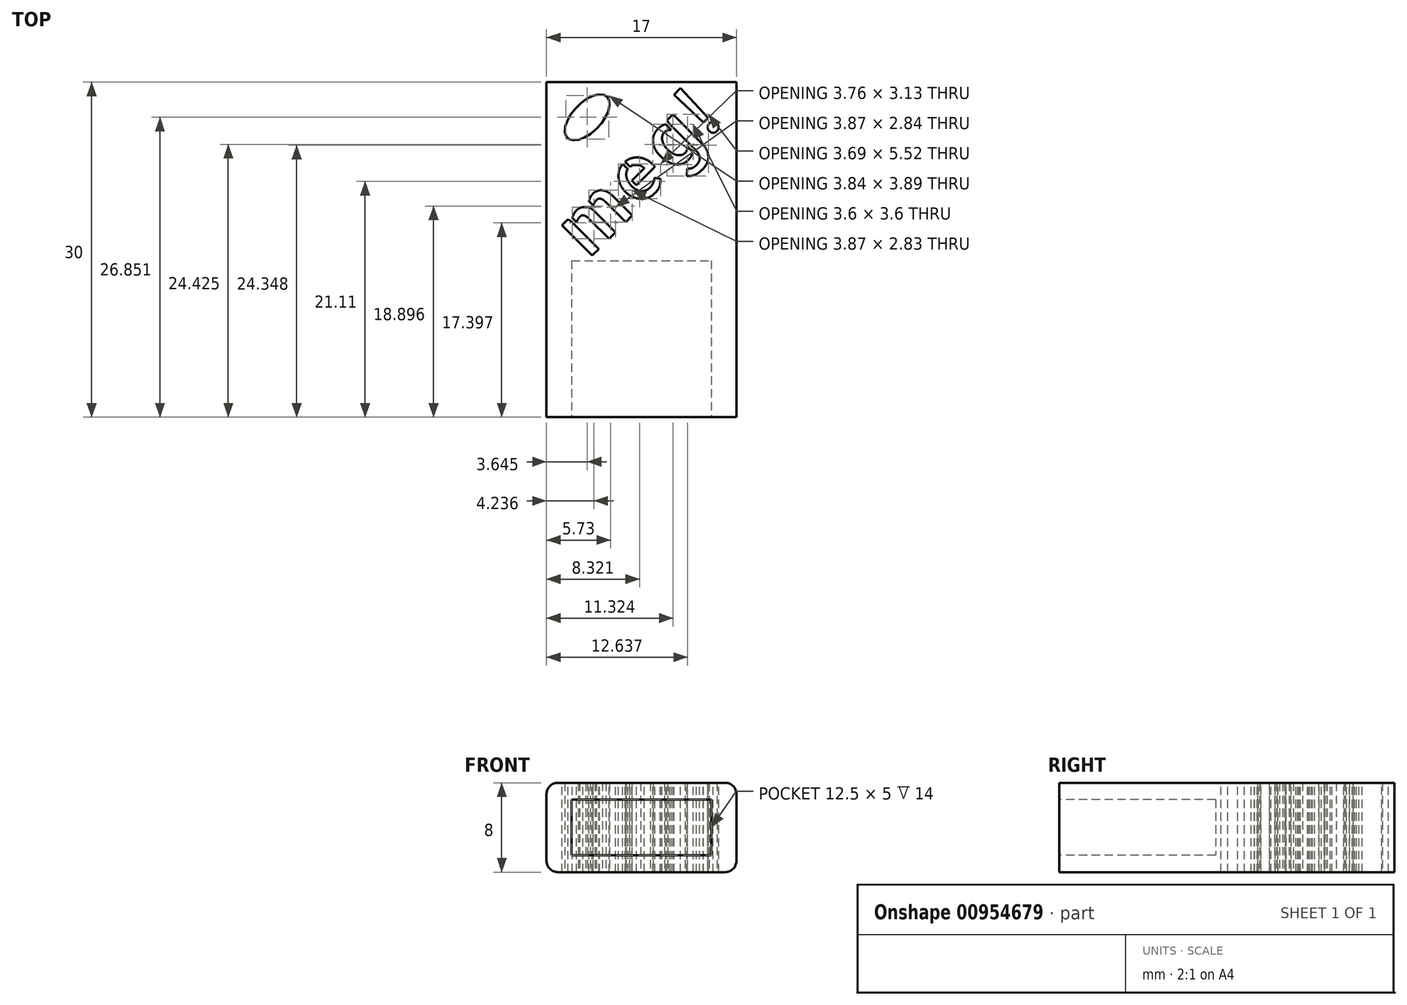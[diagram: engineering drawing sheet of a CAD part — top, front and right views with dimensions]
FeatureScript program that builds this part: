
annotation { "Feature Type Name" : "Feature", "Feature Type Description" : "" }
export const myFeature = defineFeature(function(context is Context, id is Id, definition is map)
    precondition{}
    {
        {
            var Q0;
            Q0=qCreatedBy(makeId("Front.planeOp"),FACE);
            var sketch = newSketch(context, id + "F0", { "sketchPlane" : qUnion([Q0])});
            skLineSegment(sketch, "E0.bottom", {"start": v(-7.5, 4) * mm, "end": v(7.5, 4) * mm});
            skLineSegment(sketch, "E0.top", {"start": v(-7.5, -4) * mm, "end": v(7.5, -4) * mm});
            skLineSegment(sketch, "E0.left", {"start": v(-8.5, 3) * mm, "end": v(-8.5, -3) * mm});
            skLineSegment(sketch, "E0.right", {"start": v(8.5, 3) * mm, "end": v(8.5, -3) * mm});
            skPoint(sketch, "E1.visualSharp", {"position": v(-8.5, 4) * mm});
            skArc(sketch, "E1.filletArc", {"start": v(-7.5, 4) * mm, "mid": v(-8.2, 3.7) * mm, "end": v(-8.5, 3) * mm});
            skPoint(sketch, "E2.visualSharp", {"position": v(-8.5, -4) * mm});
            skArc(sketch, "E2.filletArc", {"start": v(-8.5, -3) * mm, "mid": v(-8.2, -3.7) * mm, "end": v(-7.5, -4) * mm});
            skPoint(sketch, "E3.visualSharp", {"position": v(8.5, -4) * mm});
            skArc(sketch, "E3.filletArc", {"start": v(7.5, -4) * mm, "mid": v(8.2, -3.7) * mm, "end": v(8.5, -3) * mm});
            skPoint(sketch, "E4.visualSharp", {"position": v(8.5, 4) * mm});
            skArc(sketch, "E4.filletArc", {"start": v(8.5, 3) * mm, "mid": v(8.2, 3.7) * mm, "end": v(7.5, 4) * mm});
            skSolve(sketch);
        }
        {
            var Q0;
            Q0=makeQuery(id+"F0.imprint","IMPRINT",FACE,{"disambiguationData":[TD([[makeQuery(id+"F0.imprint","IMPRINT",EDGE,{"derivedFrom":sQuery(id+"F0.wireOp",EDGE,"E0.bottom")}),-1.0]])]});
            extrude(context, id + "F1", {"entities" : qUnion([Q0]), "depth" : 30 * mm, "offsetDistance" : 25 * mm});
        }
        {
            var Q0;
            Q0=makeQuery(id+"F1.opExtrude","CAP_FACE",FACE,{"disambiguationData":[OSD([sQuery(id+"F0.wireOp",EDGE,"E0.bottom"),sQuery(id+"F0.wireOp",EDGE,"E0.top"),sQuery(id+"F0.wireOp",EDGE,"E0.left"),sQuery(id+"F0.wireOp",EDGE,"E0.right"),sQuery(id+"F0.wireOp",EDGE,"E1.filletArc"),sQuery(id+"F0.wireOp",EDGE,"E2.filletArc"),sQuery(id+"F0.wireOp",EDGE,"E3.filletArc"),sQuery(id+"F0.wireOp",EDGE,"E4.filletArc")])],"isStart":false});
            var sketch = newSketch(context, id + "F2", { "sketchPlane" : qUnion([Q0])});
            skLineSegment(sketch, "E5.bottom", {"start": v(-6.25, 2.5) * mm, "end": v(6.25, 2.5) * mm});
            skLineSegment(sketch, "E5.top", {"start": v(-6.25, -2.5) * mm, "end": v(6.25, -2.5) * mm});
            skLineSegment(sketch, "E5.left", {"start": v(-6.25, 2.5) * mm, "end": v(-6.25, -2.5) * mm});
            skLineSegment(sketch, "E5.right", {"start": v(6.25, 2.5) * mm, "end": v(6.25, -2.5) * mm});
            skSolve(sketch);
        }
        {
            var Q0;
            Q0=makeQuery(id+"F2.imprint","IMPRINT",FACE,{"disambiguationData":[TD([[makeQuery(id+"F2.imprint","IMPRINT",EDGE,{"derivedFrom":sQuery(id+"F2.wireOp",EDGE,"E5.bottom")}),-1.0]])]});
            extrude(context, id + "F3", {"entities" : qUnion([Q0]), "operationType" : NewBodyOperationType.REMOVE, "oppositeDirection" : true, "depth" : 14 * mm, "offsetDistance" : 25 * mm});
        }
        {
            var Q0;
            Q0=makeQuery(id+"F1.opExtrude","SWEPT_BODY",BODY,{"disambiguationData":[OSD([sQuery(id+"F0.wireOp",EDGE,"E0.bottom"),sQuery(id+"F0.wireOp",EDGE,"E0.top"),sQuery(id+"F0.wireOp",EDGE,"E0.left"),sQuery(id+"F0.wireOp",EDGE,"E0.right"),sQuery(id+"F0.wireOp",EDGE,"E1.filletArc"),sQuery(id+"F0.wireOp",EDGE,"E2.filletArc"),sQuery(id+"F0.wireOp",EDGE,"E3.filletArc"),sQuery(id+"F0.wireOp",EDGE,"E4.filletArc")])]});
            var Q1;
            Q1=makeQuery(id+"F1.opExtrude","CAP_EDGE",EDGE,{"disambiguationData":[OSD([sQuery(id+"F0.wireOp",EDGE,"E0.left")])],"isStart":true});
            transform(context, id + "F4", {"entities" : qUnion([Q0]), "transformType" : TransformType.ROTATION, "transformAxis" : qUnion([Q1]), "angle" : 270 * degree, "makeCopy" : false});
        }
        {
            var Q0;
            Q0=makeQuery(id+"F1.opExtrude","SWEPT_FACE",FACE,{"disambiguationData":[OSD([sQuery(id+"F0.wireOp",EDGE,"E0.bottom")])]});
            var sketch = newSketch(context, id + "F5", { "sketchPlane" : qUnion([Q0])});
            skEllipse(sketch, "E6", {"center": v(-5.35, 3.64) * mm, "majorRadius": 2.55 * mm, "minorRadius": 1.31 * mm, "majorAxis": v(-0.72, 0.7)});
            skSolve(sketch);
        }
        {
            var Q0;
            Q0=makeQuery(id+"F5.imprint","IMPRINT",FACE,{"disambiguationData":[TD([[makeQuery(id+"F5.imprint","IMPRINT",EDGE,{"derivedFrom":sQuery(id+"F5.wireOp",EDGE,"E6")}),1.0]])]});
            extrude(context, id + "F6", {"entities" : qUnion([Q0]), "operationType" : NewBodyOperationType.REMOVE, "oppositeDirection" : true, "depth" : 10 * mm, "offsetDistance" : 25 * mm});
        }
        {
            var Q0;
            Q0=makeQuery(id+"F1.opExtrude","SWEPT_BODY",BODY,{"disambiguationData":[OSD([sQuery(id+"F0.wireOp",EDGE,"E0.bottom"),sQuery(id+"F0.wireOp",EDGE,"E0.top"),sQuery(id+"F0.wireOp",EDGE,"E0.left"),sQuery(id+"F0.wireOp",EDGE,"E0.right"),sQuery(id+"F0.wireOp",EDGE,"E1.filletArc"),sQuery(id+"F0.wireOp",EDGE,"E2.filletArc"),sQuery(id+"F0.wireOp",EDGE,"E3.filletArc"),sQuery(id+"F0.wireOp",EDGE,"E4.filletArc")])]});
            var Q1;
            Q1=makeQuery(id+"F1.opExtrude","CAP_EDGE",EDGE,{"disambiguationData":[OSD([sQuery(id+"F0.wireOp",EDGE,"E0.left")])],"isStart":true});
            transform(context, id + "F7", {"entities" : qUnion([Q0]), "transformType" : TransformType.ROTATION, "transformAxis" : qUnion([Q1]), "angle" : 90 * degree, "makeCopy" : false});
        }
        {
            var Q0;
            Q0=makeQuery(id+"F1.opExtrude","SWEPT_FACE",FACE,{"disambiguationData":[OSD([sQuery(id+"F0.wireOp",EDGE,"E0.bottom")])]});
            var sketch = newSketch(context, id + "F8", { "sketchPlane" : qUnion([Q0])});
            skText(sketch, "E7", { "text": "meg!", "fontName": "AllertaStencil-Regular.ttf"});
            const initialGuessF8  = {"E7": [-0.00482, -0.01593, 0.7071, 0.7071, 0.005]};
            skSetInitialGuess(sketch, initialGuessF8);
            skSolve(sketch);
        }
        {
            var Q0;
            Q0 = qSketchRegion(id + "F8", true);
            extrude(context, id + "F9", {"entities" : qUnion([Q0]), "operationType" : NewBodyOperationType.REMOVE, "oppositeDirection" : true, "depth" : 10 * mm, "offsetDistance" : 25 * mm});
        }
    });
